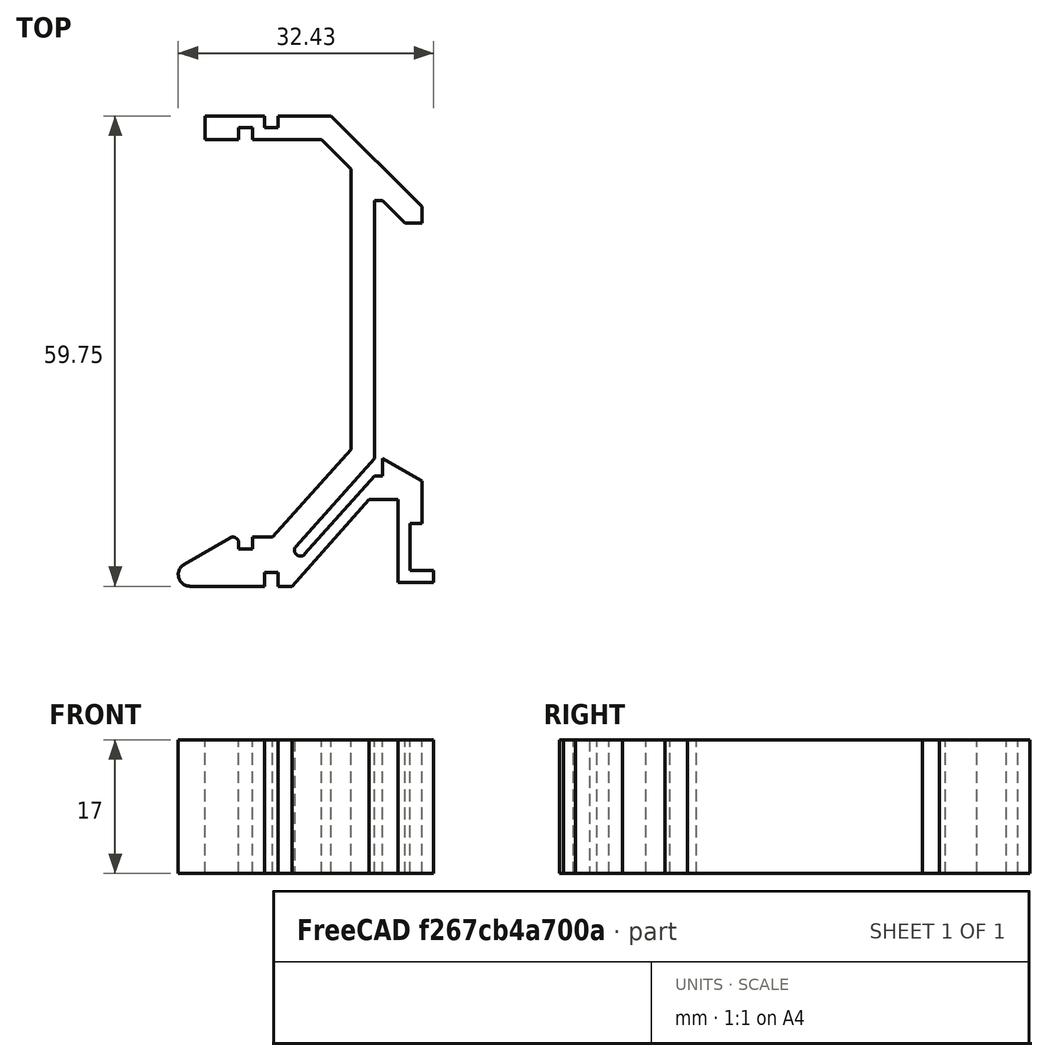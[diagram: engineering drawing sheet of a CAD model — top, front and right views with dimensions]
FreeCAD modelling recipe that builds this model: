
FCSTD DOCUMENT
Label: DIN_Mega2560
License: CC-BY 3.0
LicenseURL: http://creativecommons.org/licenses/by/3.0/
objects: Sketcher::SketchObject×1, PartDesign::Pad×1
note: 3 computed .brp shape members not serialized (recipe doc carries the construction recipe); baked Part::Feature solids carry a one-line shape summary decoded from their .brp

FEATURE [Sketcher::SketchObject] Sketch
  sketch-geometry (47):
    g0: LineSegment StartX=0 StartY=17.5 StartZ=0 EndX=0 EndY=-15.249 EndZ=0
    g1: LineSegment StartX=-21.5 StartY=25.25 StartZ=0 EndX=-17.25 EndY=25.25 EndZ=0
    g2: LineSegment StartX=-17.25 StartY=25.25 StartZ=0 EndX=-17.25 EndY=26.75 EndZ=0
    g3: LineSegment StartX=-17.25 StartY=26.75 StartZ=0 EndX=-15.5 EndY=26.75 EndZ=0
    g4: LineSegment StartX=-15.5 StartY=26.75 StartZ=0 EndX=-15.5 EndY=25.25 EndZ=0
    g5: LineSegment StartX=-15.5 StartY=25.25 StartZ=0 EndX=-6.75 EndY=25.25 EndZ=0
    g6: LineSegment StartX=-6.75 StartY=25.25 StartZ=0 EndX=-3 EndY=21.5 EndZ=0
    g7: LineSegment StartX=-3 StartY=21.5 StartZ=0 EndX=-3 EndY=-14.1038 EndZ=0
    g8: LineSegment StartX=-3 StartY=-14.1038 StartZ=0 EndX=-12.9613 EndY=-25.25 EndZ=0
    g9: LineSegment StartX=-12.9613 StartY=-25.25 StartZ=0 EndX=-15.5 EndY=-25.25 EndZ=0
    g10: LineSegment StartX=-15.5 StartY=-25.25 StartZ=0 EndX=-15.5 EndY=-26.75 EndZ=0
    g11: LineSegment StartX=-15.5 StartY=-26.75 StartZ=0 EndX=-17.25 EndY=-26.75 EndZ=0
    g12: LineSegment StartX=-18.375 StartY=-25.3505 StartZ=0 EndX=-24.1782 EndY=-28.701 EndZ=0
    g13: LineSegment StartX=-23.4282 StartY=-31.5 StartZ=0 EndX=-14 EndY=-31.5 EndZ=0
    g14: LineSegment StartX=-14 StartY=-31.5 StartZ=0 EndX=-14 EndY=-29.75 EndZ=0
    g15: LineSegment StartX=-14 StartY=-29.75 StartZ=0 EndX=-12.25 EndY=-29.75 EndZ=0
    g16: LineSegment StartX=-10.5 StartY=-31.5 StartZ=0 EndX=-0.669356 EndY=-20.5 EndZ=0
    g17: LineSegment StartX=-0.669356 StartY=-20.5 StartZ=0 EndX=3 EndY=-20.5 EndZ=0
    g18: LineSegment StartX=3 StartY=-31 StartZ=0 EndX=7.5 EndY=-31 EndZ=0
    g19: LineSegment StartX=6 StartY=-18.1368 StartZ=0 EndX=1 EndY=-15.25 EndZ=0
    g20: LineSegment StartX=1 StartY=-15.25 StartZ=0 EndX=1 EndY=-17.5 EndZ=0
    g21: LineSegment StartX=1 StartY=-17.5 StartZ=0 EndX=0 EndY=-17.5 EndZ=0
    g22: LineSegment StartX=0 StartY=-17.5 StartZ=0 EndX=-8.86463 EndY=-27.4191 EndZ=0
    g23: LineSegment StartX=-9.98307 StartY=-26.4195 StartZ=0 EndX=0 EndY=-15.249 EndZ=0
    g24: LineSegment StartX=-21.5 StartY=25.25 StartZ=0 EndX=-21.5 EndY=28.25 EndZ=0
    g25: LineSegment StartX=-21.5 StartY=28.25 StartZ=0 EndX=-14 EndY=28.25 EndZ=0
    g26: LineSegment StartX=6 StartY=14.6213 StartZ=0 EndX=3.87868 EndY=14.6213 EndZ=0
    g27: LineSegment StartX=3.87868 StartY=14.6213 StartZ=0 EndX=1 EndY=17.5 EndZ=0
    g28: LineSegment StartX=1 StartY=17.5 StartZ=0 EndX=0 EndY=17.5 EndZ=0
    g29: LineSegment StartX=-12.25 StartY=-29.75 StartZ=0 EndX=-12.25 EndY=-31.5 EndZ=0
    g30: LineSegment StartX=-5.50736 StartY=28.25 StartZ=0 EndX=6 EndY=16.7426 EndZ=0
    g31: LineSegment StartX=6 StartY=16.7426 StartZ=0 EndX=6 EndY=14.6213 EndZ=0
    g32: LineSegment StartX=3 StartY=-20.5 StartZ=0 EndX=3 EndY=-31 EndZ=0
    g33: LineSegment StartX=6 StartY=-18.1368 StartZ=0 EndX=6 EndY=-23.5 EndZ=0
    g34: LineSegment StartX=6 StartY=-23.5 StartZ=0 EndX=4.5 EndY=-23.5 EndZ=0
    g35: LineSegment StartX=4.5 StartY=-23.5 StartZ=0 EndX=4.5 EndY=-29.5 EndZ=0
    g36: LineSegment StartX=4.5 StartY=-29.5 StartZ=0 EndX=7.5 EndY=-29.5 EndZ=0
    g37: LineSegment StartX=7.5 StartY=-29.5 StartZ=0 EndX=7.5 EndY=-31 EndZ=0
    g38: LineSegment StartX=-12.25 StartY=28.25 StartZ=0 EndX=-12.25 EndY=26.75 EndZ=0
    g39: LineSegment StartX=-12.25 StartY=26.75 StartZ=0 EndX=-14 EndY=26.75 EndZ=0
    g40: LineSegment StartX=-14 StartY=26.75 StartZ=0 EndX=-14 EndY=28.25 EndZ=0
    g41: LineSegment StartX=-12.25 StartY=28.25 StartZ=0 EndX=-5.50736 EndY=28.25 EndZ=0
    g42: ArcOfCircle CenterX=-18 CenterY=-26 CenterZ=0 NormalX=0 NormalY=0 NormalZ=1 Radius=0.75 StartAngle=1.53e-10 EndAngle=2.0944
    g43: LineSegment StartX=-17.25 StartY=-26 StartZ=0 EndX=-17.25 EndY=-26.75 EndZ=0
    g44: LineSegment StartX=-12.25 StartY=-31.5 StartZ=0 EndX=-10.5 EndY=-31.5 EndZ=0
    g45: ArcOfCircle CenterX=-23.4282 CenterY=-30 CenterZ=0 NormalX=0 NormalY=0 NormalZ=1 Radius=1.5 StartAngle=2.0944 EndAngle=4.71239
    g46: ArcOfCircle CenterX=-9.42385 CenterY=-26.9193 CenterZ=0 NormalX=0 NormalY=0 NormalZ=1 Radius=0.75 StartAngle=2.41228 EndAngle=5.55385
  constraints (140):
    c: PointOnObject(g0,g-2)
    c: Vertical(g0)
    c: DistanceY(g0) = 17.5
    c: Coincident(g1,g2)
    c: Coincident(g2,g3)
    c: Coincident(g3,g4)
    c: Coincident(g4,g5)
    c: Horizontal(g5)
    c: Coincident(g5,g6)
    c: Coincident(g6,g7)
    c: Vertical(g7)
    c: Coincident(g7,g8)
    c: Coincident(g8,g9)
    c: Coincident(g9,g10)
    c: Vertical(g10)
    c: Coincident(g10,g11)
    c: Horizontal(g11)
    c: Horizontal(g13)
    c: Coincident(g13,g14)
    c: Vertical(g14)
    c: Coincident(g14,g15)
    c: Horizontal(g15)
    c: Coincident(g16,g17)
    c: Horizontal(g17)
    c: Vertical(g20)
    c: Coincident(g20,g21)
    c: Horizontal(g21)
    c: Coincident(g21,g22)
    c: Coincident(g23,g0)
    c: Coincident(g1,g24)
    c: Vertical(g24)
    c: Coincident(g24,g25)
    c: Horizontal(g25)
    c: Horizontal(g26)
    c: Coincident(g26,g27)
    c: Coincident(g27,g28)
    c: Coincident(g28,g0)
    c: Horizontal(g28)
    c: DistanceX(g6) = -3
    c: Horizontal(g9)
    c: Parallel(g23,g8)
    c: DistanceX(g9) = -15.5
    c: DistanceY(g10) = -26.75
    c: DistanceX(g9,g11) = -1.75
    c: Distance(g7,g23) = 3
    c: Parallel(g22,g23)
    c: Parallel(g16,g22)
    c: DistanceY(g10) = -1.5
    c: Distance(g22,g23) = 1.5
    c: Distance(g22,g16) = 1.5
    c: DistanceX(g14,g10) = -1.5
    c: DistanceY(g10,g14) = -3
    c: Coincident(g15,g29)
    c: Vertical(g29)
    c: Equal(g14,g15)
    c: Equal(g15,g11)
    c: Horizontal(g18)
    c: Angle(g0,g27) = 0.785398
    c: DistanceX(g28) = -1
    c: Coincident(g30,g31)
    c: Coincident(g31,g26)
    c: Vertical(g31)
    c: Equal(g31,g26)
    c: Parallel(g27,g30)
    c: Distance(g17,g21) = 3
    c: DistanceY(g41,g5) = -3
    c: Horizontal(g3)
    c: Horizontal(g1)
    c: Vertical(g2)
    c: Vertical(g4)
    c: DistanceY(g4) = -1.5
    c: DistanceX(g4) = -15.5
    c: DistanceY(g10,g3) = 53.5
    c: Distance(g26,g30) = 3
    c: DistanceY(g20) = -17.5
    c: Equal(g21,g28)
    c: DistanceX(g26) = 6
    c: DistanceX(g19) = 6
    c: Angle(g19,g0) = 2.0944
    c: Coincident(g32,g17)
    c: Coincident(g32,g18)
    c: Vertical(g32)
    c: Coincident(g19,g33)
    c: Vertical(g33)
    c: Coincident(g33,g34)
    c: Horizontal(g34)
    c: Coincident(g34,g35)
    c: Vertical(g35)
    c: Coincident(g35,g36)
    c: Horizontal(g36)
    c: Coincident(g36,g37)
    c: Coincident(g37,g18)
    c: Vertical(g37)
    c: DistanceX(g34) = -1.5
    c: DistanceX(g20) = 1
    c: Coincident(g38,g39)
    c: Coincident(g39,g40)
    c: Horizontal(g39)
    c: Vertical(g38)
    c: Vertical(g40)
    c: Tangent(g25,g41)
    c: Coincident(g40,g25)
    c: Coincident(g38,g41)
    c: Equal(g4,g40)
    c: DistanceX(g3,g39) = 1.5
    c: Tangent(g12,g42)
    c: Radius(g42) = 0.75
    c: Coincident(g43,g42)
    c: Coincident(g43,g11)
    c: Vertical(g43)
    c: DistanceY(g42,g11) = -0.75
    c: DistanceY(g37) = -1.5
    c: DistanceY(g35) = -6
    c: Coincident(g44,g29)
    c: Coincident(g44,g16)
    c: Horizontal(g44)
    c: Equal(g29,g14)
    c: Angle(g13,g12) = 0.523599
    c: Equal(g44,g29)
    c: DistanceX(g3) = 1.75
    c: Equal(g4,g2)
    c: Distance(g17,g33) = 3
    c: DistanceX(g18) = 4.5
    c: DistanceY(g32) = -10.5
    c: Coincident(g20,g19)
    c: DistanceY(g20) = -2.25
    c: DistanceX(g1) = -21.5
    c: Distance(g6,g30) = 3
    c: Tangent(g12,g45)
    c: Tangent(g13,g45)
    c: Radius(g45) = 1.5
    c: Coincident(g46,g23)
    c: Coincident(g46,g22)
    c: Tangent(g46,g23)
    c: Tangent(g46,g22)
    c: Equal(g38,g40)
    c: Equal(g3,g39)
    c: Distance(g46,g15) = 4
    c: Coincident(g30,g41)
    c: Tangent(g42,g43)
FEATURE [PartDesign::Pad] Pad  label="DIN Mega bracket"
  Length = 17
  Length2 = 100
  Sketch = -> Sketch
  Type = 0
